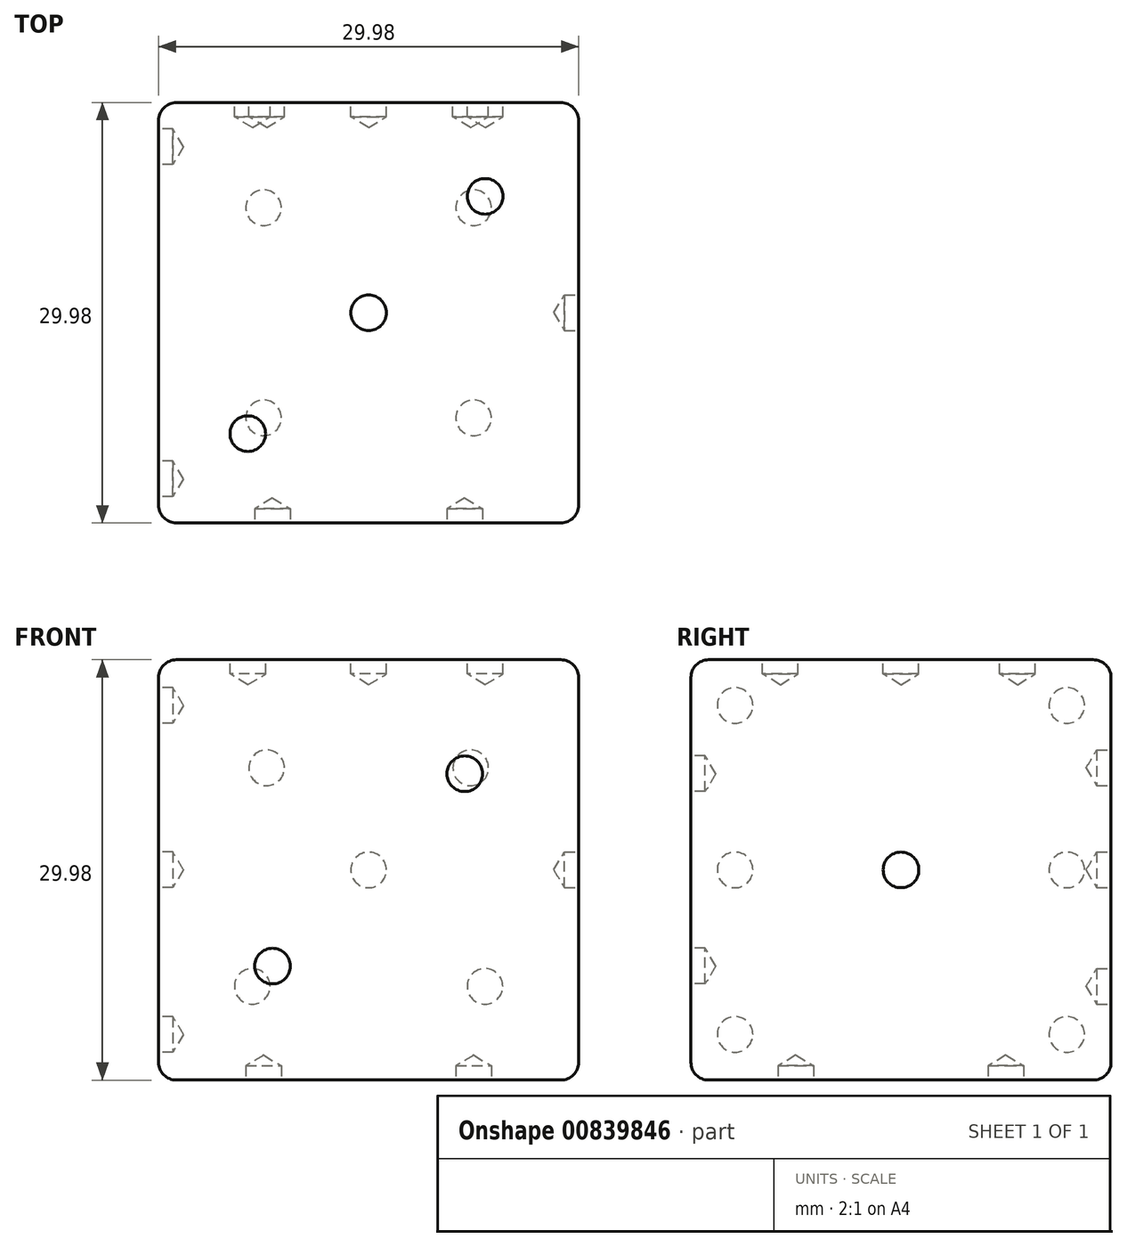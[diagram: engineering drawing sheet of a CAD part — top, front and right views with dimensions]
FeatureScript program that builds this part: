
annotation { "Feature Type Name" : "Feature", "Feature Type Description" : "" }
export const myFeature = defineFeature(function(context is Context, id is Id, definition is map)
    precondition{}
    {
        {
            var Q0;
            Q0=qCreatedBy(makeId("Front.planeOp"),FACE);
            var sketch = newSketch(context, id + "F0", { "sketchPlane" : qUnion([Q0])});
            skLineSegment(sketch, "E0.bottom", {"start": v(14.99, -14.99) * mm, "end": v(-14.99, -14.99) * mm});
            skLineSegment(sketch, "E0.top", {"start": v(14.99, 14.99) * mm, "end": v(-14.99, 14.99) * mm});
            skLineSegment(sketch, "E0.left", {"start": v(14.99, -14.99) * mm, "end": v(14.99, 14.99) * mm});
            skLineSegment(sketch, "E0.right", {"start": v(-14.99, -14.99) * mm, "end": v(-14.99, 14.99) * mm});
            skPoint(sketch, "E0.middle", {"position": v(0, 0) * mm});
            skSolve(sketch);
        }
        {
            var Q0;
            Q0 = qSketchRegion(id + "F0", true);
            extrude(context, id + "F1", {"entities" : qUnion([Q0]), "endBound" : BoundingType.SYMMETRIC, "depth" : 29.97 * mm, "offsetDistance" : 25.4 * mm});
        }
        {
            var Q0;
            Q0=makeQuery(id+"F1.opExtrude","SWEPT_EDGE",EDGE,{"disambiguationData":[OSD([sQuery(id+"F0.wireOp",EDGE,"E0.top"),sQuery(id+"F0.wireOp",EDGE,"E0.left")])]});
            var Q1;
            Q1=makeQuery(id+"F1.opExtrude","CAP_EDGE",EDGE,{"disambiguationData":[OSD([sQuery(id+"F0.wireOp",EDGE,"E0.top")])],"isStart":false});
            var Q2;
            Q2=makeQuery(id+"F1.opExtrude","SWEPT_FACE",FACE,{"disambiguationData":[OSD([sQuery(id+"F0.wireOp",EDGE,"E0.top")])]});
            var Q3;
            Q3=makeQuery(id+"F1.opExtrude","CAP_EDGE",EDGE,{"disambiguationData":[OSD([sQuery(id+"F0.wireOp",EDGE,"E0.top")])],"isStart":true});
            var Q4;
            Q4=makeQuery(id+"F1.opExtrude","CAP_EDGE",EDGE,{"disambiguationData":[OSD([sQuery(id+"F0.wireOp",EDGE,"E0.left")])],"isStart":true});
            var Q5;
            Q5=makeQuery(id+"F1.opExtrude","CAP_EDGE",EDGE,{"disambiguationData":[OSD([sQuery(id+"F0.wireOp",EDGE,"E0.left")])],"isStart":false});
            var Q6;
            Q6=makeQuery(id+"F1.opExtrude","CAP_EDGE",EDGE,{"disambiguationData":[OSD([sQuery(id+"F0.wireOp",EDGE,"E0.right")])],"isStart":false});
            var Q7;
            Q7=makeQuery(id+"F1.opExtrude","SWEPT_EDGE",EDGE,{"disambiguationData":[OSD([sQuery(id+"F0.wireOp",EDGE,"E0.bottom"),sQuery(id+"F0.wireOp",EDGE,"E0.right")])]});
            var Q8;
            Q8=makeQuery(id+"F1.opExtrude","CAP_EDGE",EDGE,{"disambiguationData":[OSD([sQuery(id+"F0.wireOp",EDGE,"E0.right")])],"isStart":true});
            var Q9;
            Q9=makeQuery(id+"F1.opExtrude","CAP_EDGE",EDGE,{"disambiguationData":[OSD([sQuery(id+"F0.wireOp",EDGE,"E0.bottom")])],"isStart":false});
            var Q10;
            Q10=makeQuery(id+"F1.opExtrude","SWEPT_EDGE",EDGE,{"disambiguationData":[OSD([sQuery(id+"F0.wireOp",EDGE,"E0.bottom"),sQuery(id+"F0.wireOp",EDGE,"E0.left")])]});
            var Q11;
            Q11=makeQuery(id+"F1.opExtrude","SWEPT_FACE",FACE,{"disambiguationData":[OSD([sQuery(id+"F0.wireOp",EDGE,"E0.bottom")])]});
            fillet(context, id + "F2", {"entities" : qUnion([Q0, Q1, Q2, Q3, Q4, Q5, Q6, Q7, Q8, Q9, Q10, Q11]), "radius" : 1.27 * mm, "tangentPropagation" : true, "allowEdgeOverflow" : false});
        }
        {
            var Q0;
            Q0=makeQuery(id+"F1.opExtrude","SWEPT_FACE",FACE,{"disambiguationData":[OSD([sQuery(id+"F0.wireOp",EDGE,"E0.bottom")])]});
            var sketch = newSketch(context, id + "F3", { "sketchPlane" : qUnion([Q0])});
            skLineSegment(sketch, "E1.bottom", {"start": v(-7.5, 7.5) * mm, "end": v(7.5, 7.5) * mm});
            skLineSegment(sketch, "E1.top", {"start": v(-7.5, -7.5) * mm, "end": v(7.5, -7.5) * mm});
            skLineSegment(sketch, "E1.left", {"start": v(-7.5, 7.5) * mm, "end": v(-7.5, -7.5) * mm});
            skLineSegment(sketch, "E1.right", {"start": v(7.5, 7.5) * mm, "end": v(7.5, -7.5) * mm});
            skPoint(sketch, "E1.middle", {"position": v(0, 0) * mm});
            skPoint(sketch, "E2", {"position": v(-7.5, 7.5) * mm});
            skPoint(sketch, "E3", {"position": v(7.5, 7.5) * mm});
            skPoint(sketch, "E4", {"position": v(7.5, -7.5) * mm});
            skPoint(sketch, "E5", {"position": v(-7.5, -7.5) * mm});
            skPoint(sketch, "E6", {"position": v(-28.5, 25.09) * mm});
            skSolve(sketch);
        }
        {
            var Q0;
            Q0=sQuery(id+"F3.wireOp",VERTEX,"E2");
            var Q1;
            Q1=sQuery(id+"F3.wireOp",VERTEX,"E3");
            var Q2;
            Q2=sQuery(id+"F3.wireOp",VERTEX,"E5");
            var Q3;
            Q3=sQuery(id+"F3.wireOp",VERTEX,"E4");
            var Q4;
            Q4=makeQuery(id+"F1.opExtrude","SWEPT_BODY",BODY,{"disambiguationData":[OSD([sQuery(id+"F0.wireOp",EDGE,"E0.bottom"),sQuery(id+"F0.wireOp",EDGE,"E0.top"),sQuery(id+"F0.wireOp",EDGE,"E0.left"),sQuery(id+"F0.wireOp",EDGE,"E0.right")])]});
            hole(context, id + "F4", {"style" : HoleStyle.SIMPLE, "endStyle" : HoleEndStyle.BLIND, "holeDiameter" : 2.54 * mm, "majorDiameter" : 6.35 * mm, "holeDepth" : 1.02 * mm, "isTappedThrough" : true, "tappedDepth" : 12.7 * mm, "tapClearance" : 3, "locations" : qUnion([Q0, Q1, Q2, Q3]), "scope" : qUnion([Q4])});
        }
        {
            var Q0;
            Q0=makeQuery(id+"F1.opExtrude","SWEPT_FACE",FACE,{"disambiguationData":[OSD([sQuery(id+"F0.wireOp",EDGE,"E0.top")])]});
            var sketch = newSketch(context, id + "F5", { "sketchPlane" : qUnion([Q0])});
            skLineSegment(sketch, "E7", {"start": v(-13.72, -13.72) * mm, "end": v(13.72, 13.72) * mm});
            skLineSegment(sketch, "E8", {"start": v(13.72, 13.72) * mm, "end": v(-13.72, -13.72) * mm});
            skPoint(sketch, "E9", {"position": v(0, 0) * mm});
            skPoint(sketch, "E10", {"position": v(8.3, 8.3) * mm});
            skPoint(sketch, "E11", {"position": v(-8.62, -8.62) * mm});
            skSolve(sketch);
        }
        {
            var Q0;
            Q0=sQuery(id+"F5.wireOp",VERTEX,"E10");
            var Q1;
            Q1=sQuery(id+"F5.wireOp",VERTEX,"E9");
            var Q2;
            Q2=sQuery(id+"F5.wireOp",VERTEX,"E11");
            var Q3;
            Q3=makeQuery(id+"F1.opExtrude","SWEPT_BODY",BODY,{"disambiguationData":[OSD([sQuery(id+"F0.wireOp",EDGE,"E0.bottom"),sQuery(id+"F0.wireOp",EDGE,"E0.top"),sQuery(id+"F0.wireOp",EDGE,"E0.left"),sQuery(id+"F0.wireOp",EDGE,"E0.right")])]});
            hole(context, id + "F6", {"style" : HoleStyle.SIMPLE, "endStyle" : HoleEndStyle.BLIND, "holeDiameter" : 2.54 * mm, "majorDiameter" : 6.35 * mm, "holeDepth" : 1.02 * mm, "isTappedThrough" : true, "tappedDepth" : 12.7 * mm, "tapClearance" : 3, "locations" : qUnion([Q0, Q1, Q2]), "scope" : qUnion([Q3])});
        }
        {
            var Q0;
            Q0=makeQuery(id+"F1.opExtrude","SWEPT_FACE",FACE,{"disambiguationData":[OSD([sQuery(id+"F0.wireOp",EDGE,"E0.right")])]});
            var sketch = newSketch(context, id + "F7", { "sketchPlane" : qUnion([Q0])});
            skLineSegment(sketch, "E12.bottom", {"start": v(11.84, -11.73) * mm, "end": v(-11.84, -11.73) * mm});
            skLineSegment(sketch, "E12.top", {"start": v(11.84, 11.73) * mm, "end": v(-11.84, 11.73) * mm});
            skLineSegment(sketch, "E12.left", {"start": v(11.84, -11.73) * mm, "end": v(11.84, 11.73) * mm});
            skLineSegment(sketch, "E12.right", {"start": v(-11.84, -11.73) * mm, "end": v(-11.84, 11.73) * mm});
            skPoint(sketch, "E12.middle", {"position": v(0, 0) * mm});
            skPoint(sketch, "E13", {"position": v(-11.84, 11.73) * mm});
            skPoint(sketch, "E14", {"position": v(11.84, 11.73) * mm});
            skPoint(sketch, "E15", {"position": v(11.84, -11.73) * mm});
            skPoint(sketch, "E16", {"position": v(-11.84, -11.73) * mm});
            skPoint(sketch, "E17", {"position": v(11.84, 0) * mm});
            skPoint(sketch, "E18", {"position": v(-11.84, 0) * mm});
            skSolve(sketch);
        }
        {
            var Q0;
            Q0=sQuery(id+"F7.wireOp",VERTEX,"E12.top.start");
            var Q1;
            Q1=sQuery(id+"F7.wireOp",VERTEX,"E17");
            var Q2;
            Q2=sQuery(id+"F7.wireOp",VERTEX,"E12.bottom.start");
            var Q3;
            Q3=sQuery(id+"F7.wireOp",VERTEX,"E16");
            var Q4;
            Q4=sQuery(id+"F7.wireOp",VERTEX,"E18");
            var Q5;
            Q5=sQuery(id+"F7.wireOp",VERTEX,"E12.top.end");
            var Q6;
            Q6=makeQuery(id+"F1.opExtrude","SWEPT_BODY",BODY,{"disambiguationData":[OSD([sQuery(id+"F0.wireOp",EDGE,"E0.bottom"),sQuery(id+"F0.wireOp",EDGE,"E0.top"),sQuery(id+"F0.wireOp",EDGE,"E0.left"),sQuery(id+"F0.wireOp",EDGE,"E0.right")])]});
            hole(context, id + "F8", {"style" : HoleStyle.SIMPLE, "endStyle" : HoleEndStyle.BLIND, "holeDiameter" : 2.54 * mm, "majorDiameter" : 6.35 * mm, "holeDepth" : 1.02 * mm, "isTappedThrough" : true, "tappedDepth" : 12.7 * mm, "tapClearance" : 3, "locations" : qUnion([Q0, Q1, Q2, Q3, Q4, Q5]), "scope" : qUnion([Q6])});
        }
        {
            var Q0;
            Q0=makeQuery(id+"F1.opExtrude","SWEPT_FACE",FACE,{"disambiguationData":[OSD([sQuery(id+"F0.wireOp",EDGE,"E0.left")])]});
            var sketch = newSketch(context, id + "F9", { "sketchPlane" : qUnion([Q0])});
            skPoint(sketch, "E19", {"position": v(0, 0) * mm});
            skSolve(sketch);
        }
        {
            var Q0;
            Q0=sQuery(id+"F9.wireOp",VERTEX,"E19");
            var Q1;
            Q1=makeQuery(id+"F1.opExtrude","SWEPT_BODY",BODY,{"disambiguationData":[OSD([sQuery(id+"F0.wireOp",EDGE,"E0.bottom"),sQuery(id+"F0.wireOp",EDGE,"E0.top"),sQuery(id+"F0.wireOp",EDGE,"E0.left"),sQuery(id+"F0.wireOp",EDGE,"E0.right")])]});
            hole(context, id + "F10", {"style" : HoleStyle.SIMPLE, "endStyle" : HoleEndStyle.BLIND, "holeDiameter" : 2.54 * mm, "majorDiameter" : 6.35 * mm, "holeDepth" : 1.02 * mm, "isTappedThrough" : true, "tappedDepth" : 12.7 * mm, "tapClearance" : 3, "locations" : qUnion([Q0]), "scope" : qUnion([Q1])});
        }
        {
            var Q0;
            Q0=makeQuery(id+"F1.opExtrude","CAP_FACE",FACE,{"disambiguationData":[OSD([sQuery(id+"F0.wireOp",EDGE,"E0.bottom"),sQuery(id+"F0.wireOp",EDGE,"E0.top"),sQuery(id+"F0.wireOp",EDGE,"E0.left"),sQuery(id+"F0.wireOp",EDGE,"E0.right")])],"isStart":true});
            var sketch = newSketch(context, id + "F11", { "sketchPlane" : qUnion([Q0])});
            skLineSegment(sketch, "E20", {"start": v(0, 0) * mm, "end": v(-13.72, 13.72) * mm});
            skLineSegment(sketch, "E21", {"start": v(-13.72, 13.72) * mm, "end": v(0, 0) * mm});
            skLineSegment(sketch, "E22", {"start": v(0, 0) * mm, "end": v(13.72, -13.72) * mm});
            skLineSegment(sketch, "E23", {"start": v(13.72, -13.72) * mm, "end": v(0, 0) * mm});
            skLineSegment(sketch, "E24", {"start": v(0, 0) * mm, "end": v(13.72, 13.72) * mm});
            skLineSegment(sketch, "E25", {"start": v(0, 0) * mm, "end": v(-13.72, -13.72) * mm});
            skLineSegment(sketch, "E26", {"start": v(-13.72, -13.72) * mm, "end": v(0, 0) * mm});
            skPoint(sketch, "E27", {"position": v(0, 0) * mm});
            skLineSegment(sketch, "E28", {"start": v(-13.72, 7.28) * mm, "end": v(13.72, 7.28) * mm});
            skLineSegment(sketch, "E29", {"start": v(13.72, 7.28) * mm, "end": v(13.72, -8.3) * mm});
            skLineSegment(sketch, "E30", {"start": v(13.72, -8.3) * mm, "end": v(-13.72, -8.3) * mm});
            skLineSegment(sketch, "E31", {"start": v(-13.72, -8.3) * mm, "end": v(-13.72, 7.28) * mm});
            skPoint(sketch, "E32", {"position": v(-7.28, 7.28) * mm});
            skPoint(sketch, "E33", {"position": v(7.28, 7.28) * mm});
            skPoint(sketch, "E34", {"position": v(8.3, -8.3) * mm});
            skPoint(sketch, "E35", {"position": v(-8.3, -8.3) * mm});
            skSolve(sketch);
        }
        {
            var Q0;
            Q0=sQuery(id+"F11.wireOp",VERTEX,"E32");
            var Q1;
            Q1=sQuery(id+"F11.wireOp",VERTEX,"E33");
            var Q2;
            Q2=sQuery(id+"F11.wireOp",VERTEX,"E27");
            var Q3;
            Q3=sQuery(id+"F11.wireOp",VERTEX,"E34");
            var Q4;
            Q4=sQuery(id+"F11.wireOp",VERTEX,"E35");
            var Q5;
            Q5=makeQuery(id+"F1.opExtrude","SWEPT_BODY",BODY,{"disambiguationData":[OSD([sQuery(id+"F0.wireOp",EDGE,"E0.bottom"),sQuery(id+"F0.wireOp",EDGE,"E0.top"),sQuery(id+"F0.wireOp",EDGE,"E0.left"),sQuery(id+"F0.wireOp",EDGE,"E0.right")])]});
            hole(context, id + "F12", {"style" : HoleStyle.SIMPLE, "endStyle" : HoleEndStyle.BLIND, "holeDiameter" : 2.54 * mm, "majorDiameter" : 6.35 * mm, "holeDepth" : 1.02 * mm, "isTappedThrough" : true, "tappedDepth" : 12.7 * mm, "tapClearance" : 3, "locations" : qUnion([Q0, Q1, Q2, Q3, Q4]), "scope" : qUnion([Q5])});
        }
        {
            var Q0;
            Q0=makeQuery(id+"F1.opExtrude","CAP_FACE",FACE,{"disambiguationData":[OSD([sQuery(id+"F0.wireOp",EDGE,"E0.bottom"),sQuery(id+"F0.wireOp",EDGE,"E0.top"),sQuery(id+"F0.wireOp",EDGE,"E0.left"),sQuery(id+"F0.wireOp",EDGE,"E0.right")])],"isStart":false});
            var sketch = newSketch(context, id + "F13", { "sketchPlane" : qUnion([Q0])});
            skLineSegment(sketch, "E36", {"start": v(0, 0) * mm, "end": v(13.72, 13.72) * mm});
            skLineSegment(sketch, "E37", {"start": v(13.72, 13.72) * mm, "end": v(-13.72, -13.72) * mm});
            skLineSegment(sketch, "E38", {"start": v(-13.72, -13.72) * mm, "end": v(0, 0) * mm});
            skPoint(sketch, "E39", {"position": v(-6.86, -6.86) * mm});
            skPoint(sketch, "E40", {"position": v(6.86, 6.86) * mm});
            skSolve(sketch);
        }
        {
            var Q0;
            Q0=sQuery(id+"F13.wireOp",VERTEX,"E40");
            var Q1;
            Q1=sQuery(id+"F13.wireOp",VERTEX,"E39");
            var Q2;
            Q2=makeQuery(id+"F1.opExtrude","SWEPT_BODY",BODY,{"disambiguationData":[OSD([sQuery(id+"F0.wireOp",EDGE,"E0.bottom"),sQuery(id+"F0.wireOp",EDGE,"E0.top"),sQuery(id+"F0.wireOp",EDGE,"E0.left"),sQuery(id+"F0.wireOp",EDGE,"E0.right")])]});
            hole(context, id + "F14", {"style" : HoleStyle.SIMPLE, "endStyle" : HoleEndStyle.BLIND, "holeDiameter" : 2.54 * mm, "majorDiameter" : 6.35 * mm, "holeDepth" : 1.02 * mm, "isTappedThrough" : true, "tappedDepth" : 12.7 * mm, "tapClearance" : 3, "locations" : qUnion([Q0, Q1]), "scope" : qUnion([Q2])});
        }
    });
